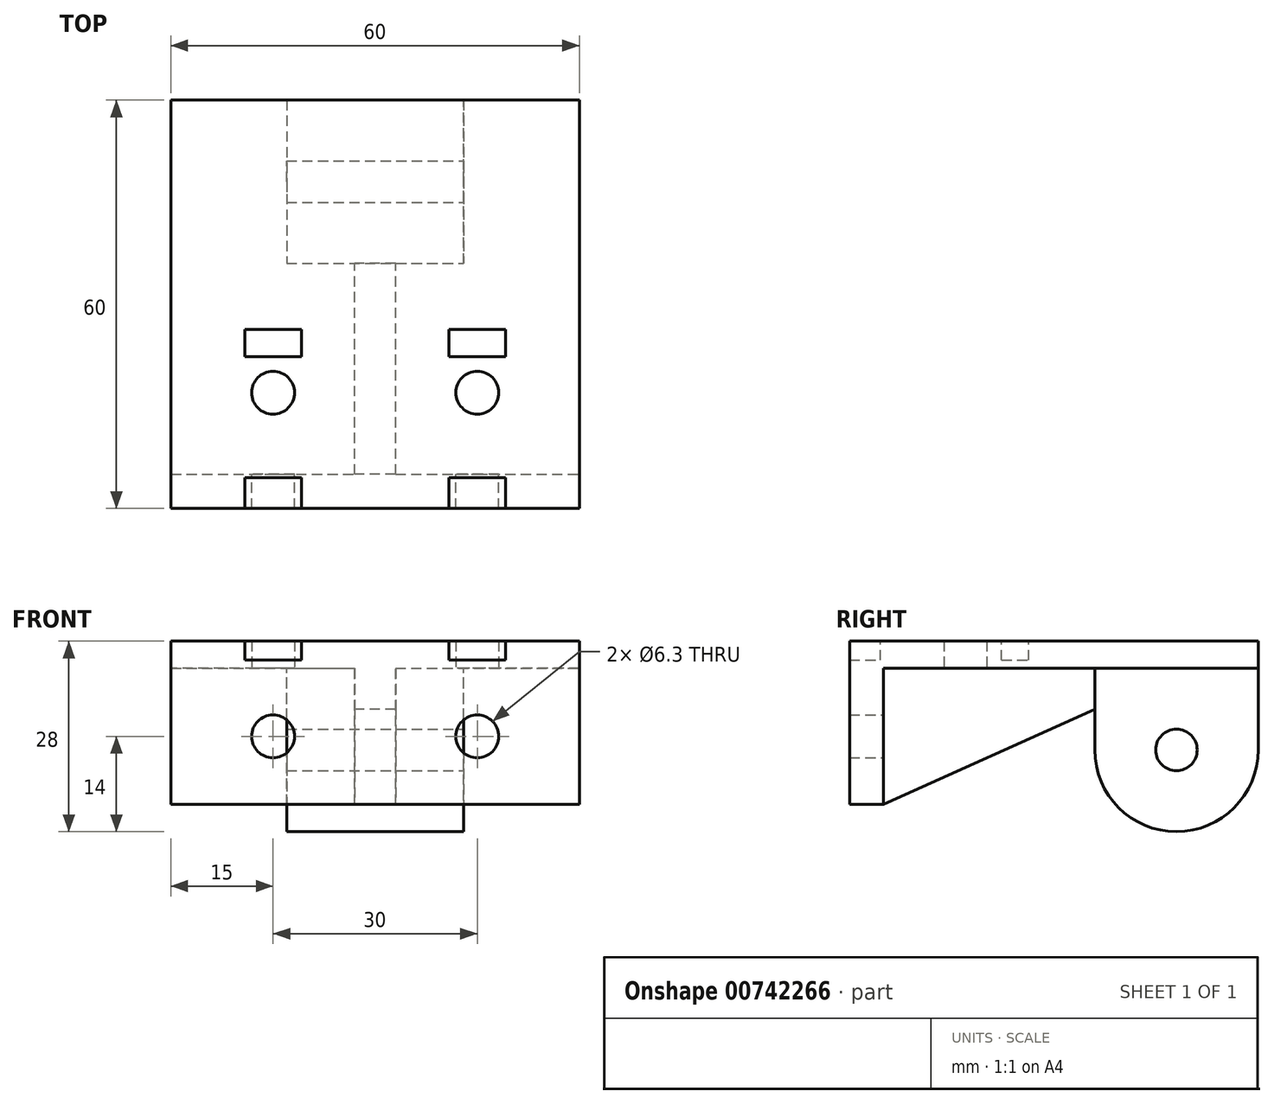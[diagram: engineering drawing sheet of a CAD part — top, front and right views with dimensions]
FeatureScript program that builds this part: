
annotation { "Feature Type Name" : "Feature", "Feature Type Description" : "" }
export const myFeature = defineFeature(function(context is Context, id is Id, definition is map)
    precondition{}
    {
        {
            var Q0;
            Q0=qCreatedBy(makeId("Top.planeOp"),FACE);
            var sketch = newSketch(context, id + "F0", { "sketchPlane" : qUnion([Q0])});
            skLineSegment(sketch, "E0.bottom", {"start": v(30, -30) * mm, "end": v(-30, -30) * mm});
            skLineSegment(sketch, "E0.top", {"start": v(30, 30) * mm, "end": v(-30, 30) * mm});
            skLineSegment(sketch, "E0.left", {"start": v(30, -30) * mm, "end": v(30, 30) * mm});
            skLineSegment(sketch, "E0.right", {"start": v(-30, -30) * mm, "end": v(-30, 30) * mm});
            skPoint(sketch, "E0.middle", {"position": v(0, 0) * mm});
            skLineSegment(sketch, "E1", {"start": v(-30, -3) * mm, "end": v(30, -3) * mm, "construction": true});
            skLineSegment(sketch, "E2", {"start": v(-15, -3) * mm, "end": v(-15, -30) * mm, "construction": true});
            skLineSegment(sketch, "E3", {"start": v(15, -3) * mm, "end": v(15, -30) * mm, "construction": true});
            skLineSegment(sketch, "E4", {"start": v(-15, -13) * mm, "end": v(15, -13) * mm, "construction": true});
            skCircle(sketch, "E5", {"center": v(-15, -13) * mm, "radius": 3.15 * mm});
            skCircle(sketch, "E6", {"center": v(15, -13) * mm, "radius": 3.15 * mm});
            skSolve(sketch);
        }
        {
            var Q0;
            Q0=makeQuery(id+"F0.imprint","IMPRINT",FACE,{"disambiguationData":[TD([[makeQuery(id+"F0.imprint","IMPRINT",EDGE,{"derivedFrom":sQuery(id+"F0.wireOp",EDGE,"E0.bottom")}),-1.0]])]});
            extrude(context, id + "F1", {"entities" : qUnion([Q0]), "depth" : 4 * mm, "offsetDistance" : 25 * mm});
        }
        {
            var Q0;
            Q0=makeQuery(id+"F1.opExtrude","CAP_FACE",FACE,{"disambiguationData":[OSD([sQuery(id+"F0.wireOp",EDGE,"E0.bottom"),sQuery(id+"F0.wireOp",EDGE,"E0.top"),sQuery(id+"F0.wireOp",EDGE,"E0.left"),sQuery(id+"F0.wireOp",EDGE,"E0.right"),sQuery(id+"F0.wireOp",EDGE,"E5"),sQuery(id+"F0.wireOp",EDGE,"E6")])],"isStart":false});
            var sketch = newSketch(context, id + "F2", { "sketchPlane" : qUnion([Q0])});
            skLineSegment(sketch, "E7.bottom", {"start": v(-10.85, -30) * mm, "end": v(-19.15, -30) * mm});
            skLineSegment(sketch, "E7.top", {"start": v(-10.85, -25.5) * mm, "end": v(-19.15, -25.5) * mm});
            skLineSegment(sketch, "E7.left", {"start": v(-10.85, -30) * mm, "end": v(-10.85, -25.5) * mm});
            skLineSegment(sketch, "E7.right", {"start": v(-19.15, -30) * mm, "end": v(-19.15, -25.5) * mm});
            skPoint(sketch, "E7.middle", {"position": v(-15, -27.75) * mm});
            skLineSegment(sketch, "E8.bottom", {"start": v(19.15, -30) * mm, "end": v(10.85, -30) * mm});
            skLineSegment(sketch, "E8.top", {"start": v(19.15, -25.5) * mm, "end": v(10.85, -25.5) * mm});
            skLineSegment(sketch, "E8.left", {"start": v(19.15, -30) * mm, "end": v(19.15, -25.5) * mm});
            skLineSegment(sketch, "E8.right", {"start": v(10.85, -30) * mm, "end": v(10.85, -25.5) * mm});
            skPoint(sketch, "E8.middle", {"position": v(15, -27.75) * mm});
            skLineSegment(sketch, "E9", {"start": v(-10.85, -25.5) * mm, "end": v(10.85, -25.5) * mm, "construction": true});
            skLineSegment(sketch, "E10.bottom", {"start": v(-10.85, -7.7) * mm, "end": v(-19.15, -7.7) * mm});
            skLineSegment(sketch, "E10.top", {"start": v(-10.85, -3.7) * mm, "end": v(-19.15, -3.7) * mm});
            skLineSegment(sketch, "E10.left", {"start": v(-10.85, -7.7) * mm, "end": v(-10.85, -3.7) * mm});
            skLineSegment(sketch, "E10.right", {"start": v(-19.15, -7.7) * mm, "end": v(-19.15, -3.7) * mm});
            skPoint(sketch, "E10.middle", {"position": v(-15, -5.7) * mm});
            skLineSegment(sketch, "E11", {"start": v(-19.15, -7.7) * mm, "end": v(-19.15, -25.5) * mm, "construction": true});
            skLineSegment(sketch, "E12.bottom", {"start": v(19.15, -7.7) * mm, "end": v(10.85, -7.7) * mm});
            skLineSegment(sketch, "E12.top", {"start": v(19.15, -3.7) * mm, "end": v(10.85, -3.7) * mm});
            skLineSegment(sketch, "E12.left", {"start": v(19.15, -7.7) * mm, "end": v(19.15, -3.7) * mm});
            skLineSegment(sketch, "E12.right", {"start": v(10.85, -7.7) * mm, "end": v(10.85, -3.7) * mm});
            skPoint(sketch, "E12.middle", {"position": v(15, -5.7) * mm});
            skLineSegment(sketch, "E13", {"start": v(-10.85, -3.7) * mm, "end": v(10.85, -3.7) * mm, "construction": true});
            skLineSegment(sketch, "E14", {"start": v(19.15, -7.7) * mm, "end": v(19.15, -25.5) * mm, "construction": true});
            skSolve(sketch);
        }
        {
            var Q0;
            Q0 = qSketchRegion(id + "F2", true);
            extrude(context, id + "F3", {"entities" : qUnion([Q0]), "operationType" : NewBodyOperationType.REMOVE, "oppositeDirection" : true, "depth" : 2.8 * mm, "offsetDistance" : 25 * mm});
        }
        {
            var Q0;
            Q0=makeQuery(id+"F1.opExtrude","CAP_FACE",FACE,{"disambiguationData":[OSD([sQuery(id+"F0.wireOp",EDGE,"E0.bottom"),sQuery(id+"F0.wireOp",EDGE,"E0.top"),sQuery(id+"F0.wireOp",EDGE,"E0.left"),sQuery(id+"F0.wireOp",EDGE,"E0.right"),sQuery(id+"F0.wireOp",EDGE,"E5"),sQuery(id+"F0.wireOp",EDGE,"E6")])],"isStart":true});
            var sketch = newSketch(context, id + "F4", { "sketchPlane" : qUnion([Q0])});
            skLineSegment(sketch, "E15.bottom", {"start": v(-13, -30) * mm, "end": v(13, -30) * mm});
            skLineSegment(sketch, "E15.top", {"start": v(-13, -6) * mm, "end": v(13, -6) * mm});
            skLineSegment(sketch, "E15.left", {"start": v(-13, -30) * mm, "end": v(-13, -6) * mm});
            skLineSegment(sketch, "E15.right", {"start": v(13, -30) * mm, "end": v(13, -6) * mm});
            skPoint(sketch, "E15.middle", {"position": v(0, -18) * mm});
            skLineSegment(sketch, "E16", {"start": v(0, -18) * mm, "end": v(0, 0) * mm, "construction": true});
            skSolve(sketch);
        }
        {
            var Q0;
            Q0=makeQuery(id+"F4.imprint","IMPRINT",FACE,{"disambiguationData":[TD([[makeQuery(id+"F4.imprint","IMPRINT",EDGE,{"derivedFrom":sQuery(id+"F4.wireOp",EDGE,"E15.bottom")}),-1.0]])]});
            extrude(context, id + "F5", {"entities" : qUnion([Q0]), "operationType" : NewBodyOperationType.ADD, "depth" : 24 * mm, "offsetDistance" : 25 * mm});
        }
        {
            var Q0;
            Q0=makeQuery(id+"F5.opExtrude","SWEPT_FACE",FACE,{"disambiguationData":[OSD([sQuery(id+"F4.wireOp",EDGE,"E15.right")])]});
            var sketch = newSketch(context, id + "F6", { "sketchPlane" : qUnion([Q0])});
            skArc(sketch, "E17", {"start": v(6, -12) * mm, "mid": v(18, -24) * mm, "end": v(30, -12) * mm});
            skLineSegment(sketch, "E18", {"start": v(18, -12) * mm, "end": v(30, -12) * mm, "construction": true});
            skLineSegment(sketch, "E19", {"start": v(6, -12) * mm, "end": v(6, -24) * mm});
            skLineSegment(sketch, "E20", {"start": v(6, -24) * mm, "end": v(30, -24) * mm});
            skLineSegment(sketch, "E21", {"start": v(30, -24) * mm, "end": v(30, -12) * mm});
            skPoint(sketch, "E22", {"position": v(6, -12) * mm});
            skCircle(sketch, "E23", {"center": v(18, -12) * mm, "radius": 3.05 * mm});
            skSolve(sketch);
        }
        {
            var Q0;
            Q0 = qSketchRegion(id + "F6", true);
            extrude(context, id + "F7", {"entities" : qUnion([Q0]), "operationType" : NewBodyOperationType.REMOVE, "endBound" : BoundingType.THROUGH_ALL, "oppositeDirection" : true, "depth" : 25 * mm, "offsetDistance" : 25 * mm});
        }
        {
            var Q0;
            Q0=makeQuery(id+"F1.opExtrude","CAP_FACE",FACE,{"disambiguationData":[OSD([sQuery(id+"F0.wireOp",EDGE,"E0.bottom"),sQuery(id+"F0.wireOp",EDGE,"E0.top"),sQuery(id+"F0.wireOp",EDGE,"E0.left"),sQuery(id+"F0.wireOp",EDGE,"E0.right"),sQuery(id+"F0.wireOp",EDGE,"E5"),sQuery(id+"F0.wireOp",EDGE,"E6")])],"isStart":true});
            var sketch = newSketch(context, id + "F8", { "sketchPlane" : qUnion([Q0])});
            skLineSegment(sketch, "E24.bottom", {"start": v(-30, 30) * mm, "end": v(30, 30) * mm});
            skLineSegment(sketch, "E24.top", {"start": v(-30, 25) * mm, "end": v(30, 25) * mm});
            skLineSegment(sketch, "E24.left", {"start": v(-30, 30) * mm, "end": v(-30, 25) * mm});
            skLineSegment(sketch, "E24.right", {"start": v(30, 30) * mm, "end": v(30, 25) * mm});
            skSolve(sketch);
        }
        {
            var Q0;
            Q0=makeQuery(id+"F8.imprint","IMPRINT",FACE,{"disambiguationData":[TD([[makeQuery(id+"F8.imprint","IMPRINT",EDGE,{"derivedFrom":sQuery(id+"F8.wireOp",EDGE,"E24.bottom")}),1.0]])]});
            extrude(context, id + "F9", {"entities" : qUnion([Q0]), "operationType" : NewBodyOperationType.ADD, "depth" : 20 * mm, "offsetDistance" : 25 * mm});
        }
        {
            var Q0;
            Q0=qCreatedBy(makeId("Right.planeOp"),FACE);
            var sketch = newSketch(context, id + "F10", { "sketchPlane" : qUnion([Q0])});
            skLineSegment(sketch, "E25", {"start": v(-25, -20) * mm, "end": v(-25, 0) * mm});
            skLineSegment(sketch, "E26", {"start": v(-25, 0) * mm, "end": v(6, 0) * mm});
            skLineSegment(sketch, "E27", {"start": v(6, 0) * mm, "end": v(6, -6) * mm});
            skLineSegment(sketch, "E28", {"start": v(6, -6) * mm, "end": v(-25, -20) * mm});
            skSolve(sketch);
        }
        {
            var Q0;
            Q0=makeQuery(id+"F10.imprint","IMPRINT",FACE,{"disambiguationData":[TD([[makeQuery(id+"F10.imprint","IMPRINT",EDGE,{"derivedFrom":sQuery(id+"F10.wireOp",EDGE,"E25")}),-1.0]])]});
            extrude(context, id + "F11", {"entities" : qUnion([Q0]), "operationType" : NewBodyOperationType.ADD, "depth" : 3 * mm, "offsetDistance" : 25 * mm, "hasSecondDirection" : true, "secondDirectionOppositeDirection" : true, "secondDirectionDepth" : 3 * mm});
        }
        {
            var Q0;
            {var subQ1=sQuery(id+"F8.wireOp",EDGE,"E24.top");var subQ2=sQuery(id+"F0.wireOp",EDGE,"E0.right");Q0=makeQuery(id+"F11.boolean.opBoolean","SPLIT",FACE,{"disambiguationData":[TD([makeQuery(id+"F1.opExtrude","SWEPT_FACE",FACE,{"disambiguationData":[OSD([subQ2])]})])],"derivedFrom":makeQuery(id+"F9.opExtrude","SWEPT_FACE",FACE,{"disambiguationData":[OSD([subQ1])]})});}
            var sketch = newSketch(context, id + "F12", { "sketchPlane" : qUnion([Q0])});
            skLineSegment(sketch, "E29", {"start": v(15, -20) * mm, "end": v(15, 0) * mm, "construction": true});
            skLineSegment(sketch, "E30", {"start": v(-15, -20) * mm, "end": v(-15, 0) * mm, "construction": true});
            skCircle(sketch, "E31", {"center": v(15, -10) * mm, "radius": 3.15 * mm});
            skCircle(sketch, "E32", {"center": v(-15, -10) * mm, "radius": 3.15 * mm});
            skSolve(sketch);
        }
        {
            var Q0;
            Q0=makeQuery(id+"F12.imprint","IMPRINT",FACE,{"disambiguationData":[TD([[makeQuery(id+"F12.imprint","IMPRINT",EDGE,{"derivedFrom":sQuery(id+"F12.wireOp",EDGE,"E31")}),1.0]])]});
            var Q1;
            Q1=makeQuery(id+"F12.imprint","IMPRINT",FACE,{"disambiguationData":[TD([[makeQuery(id+"F12.imprint","IMPRINT",EDGE,{"derivedFrom":sQuery(id+"F12.wireOp",EDGE,"E32")}),1.0]])]});
            extrude(context, id + "F13", {"entities" : qUnion([Q0, Q1]), "operationType" : NewBodyOperationType.REMOVE, "endBound" : BoundingType.THROUGH_ALL, "oppositeDirection" : true, "depth" : 25 * mm, "offsetDistance" : 25 * mm});
        }
    });
